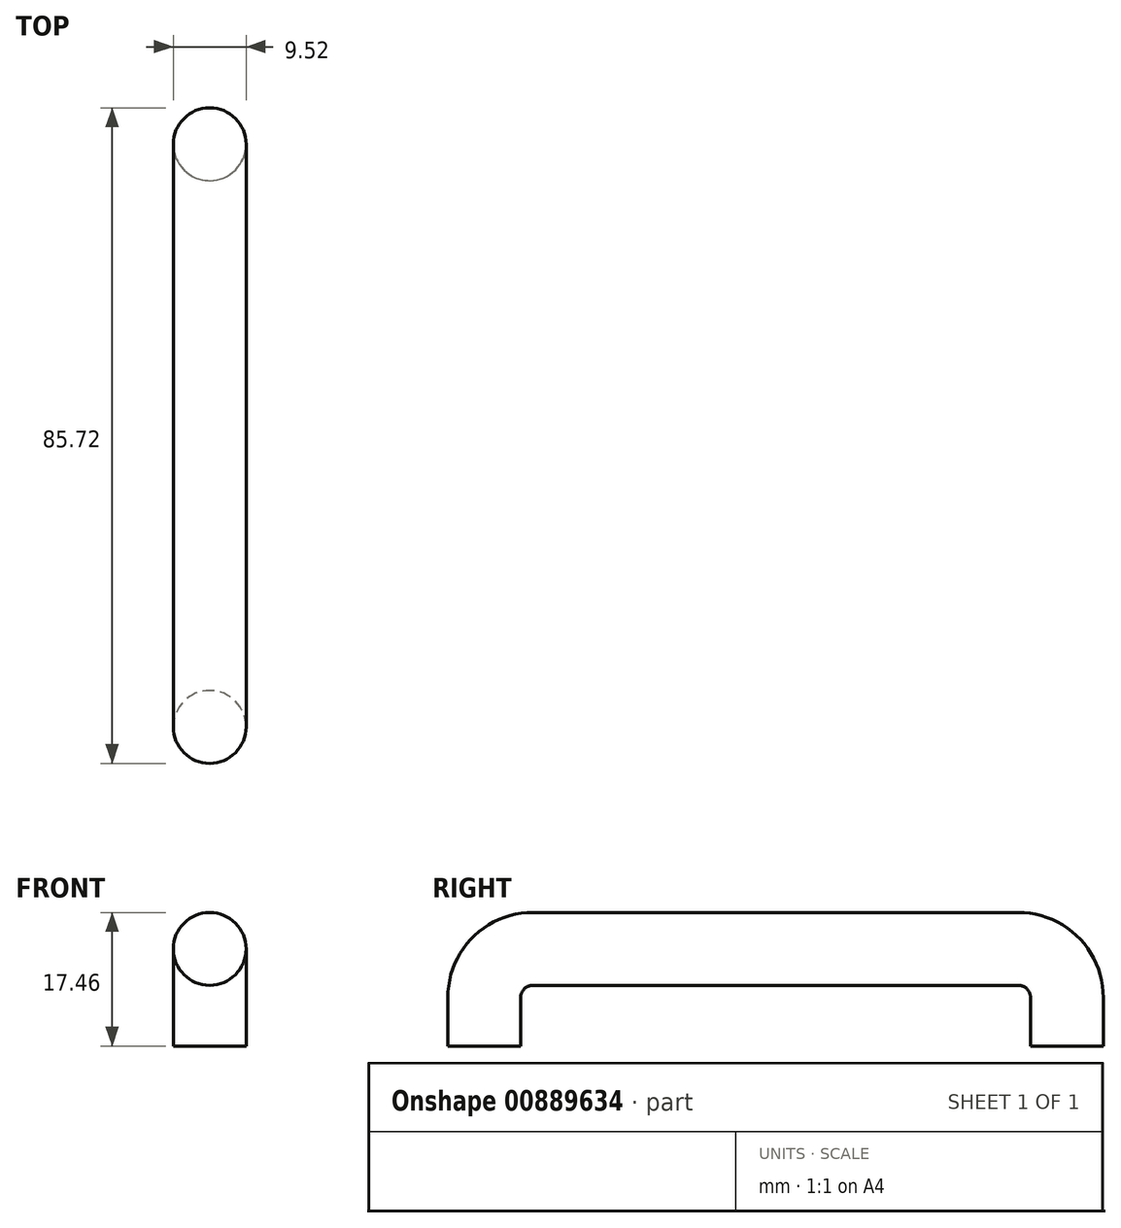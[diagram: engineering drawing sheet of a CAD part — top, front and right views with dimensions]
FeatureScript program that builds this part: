
annotation { "Feature Type Name" : "Feature", "Feature Type Description" : "" }
export const myFeature = defineFeature(function(context is Context, id is Id, definition is map)
    precondition{}
    {
        {
            var Q0;
            Q0=qCreatedBy(makeId("Right.planeOp"),FACE);
            var sketch = newSketch(context, id + "F0", { "sketchPlane" : qUnion([Q0])});
            skLineSegment(sketch, "E0", {"start": v(0, 0) * mm, "end": v(0, 6.35) * mm});
            skLineSegment(sketch, "E1", {"start": v(6.35, 12.7) * mm, "end": v(69.85, 12.7) * mm});
            skLineSegment(sketch, "E2", {"start": v(76.2, 6.35) * mm, "end": v(76.2, 0) * mm});
            skPoint(sketch, "E3.visualSharp", {"position": v(0, 12.7) * mm});
            skArc(sketch, "E3.filletArc", {"start": v(6.35, 12.7) * mm, "mid": v(1.86, 10.84) * mm, "end": v(0, 6.35) * mm});
            skPoint(sketch, "E4.visualSharp", {"position": v(76.2, 12.7) * mm});
            skArc(sketch, "E4.filletArc", {"start": v(76.2, 6.35) * mm, "mid": v(74.34, 10.84) * mm, "end": v(69.85, 12.7) * mm});
            skSolve(sketch);
        }
        {
            var Q0;
            Q0=qCreatedBy(makeId("Top.planeOp"),FACE);
            var sketch = newSketch(context, id + "F1", { "sketchPlane" : qUnion([Q0])});
            skCircle(sketch, "E5", {"center": v(0, 0) * mm, "radius": 4.76 * mm});
            skSolve(sketch);
        }
        {
            var Q0;
            Q0 = qSketchRegion(id + "F1", true);
            var Q1;
            Q1 = qConstructionFilter(qBodyType(qCreatedBy(id + "F0" ,EDGE), BodyType.WIRE), ConstructionObject.NO);
            sweep(context, id + "F2", {"profiles" : qUnion([Q0]), "path" : qUnion([Q1])});
        }
    });
